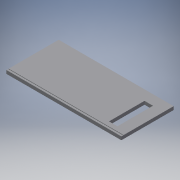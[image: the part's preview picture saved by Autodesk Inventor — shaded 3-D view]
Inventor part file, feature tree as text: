
AUTODESK INVENTOR PART (.ipt)
format: ipt  version: 2018.3 (Build 223284000, 284)  size: 119,296 bytes
history: native  units: mm
features: extrude x4, sketch x4
ambient origin geometry x8: Origin, YZ Plane, XZ Plane, XY Plane, X Axis, Y Axis, Z Axis, Center Point
bodies: Solid1 (feature_tree)
feature tree (8):
  extrude  "Extrusion1"  Depth=15.7mm
  extrude  "Extrusion3"  Depth=0.15mm
  extrude  "Extrusion4"  Depth=0.3mm TaperAngle=0.0deg
  extrude  "Extrusion5"  Depth=0.1mm
  sketch  "Sketch1"  dims[d0=34.5mm d1=15.7mm]
  sketch  "Sketch3"  dims[d2=1.0mm d3=0.0mm d8=0.15mm]
  sketch  "Sketch4"  dims[d9=0.3mm d10=7.0mm d11=0.0mm]
  sketch  "Sketch5"  dims[d12=0.4mm d13=0.1mm d14=0.15mm d15=0.0mm d16=1.0mm d17=0.0mm]
